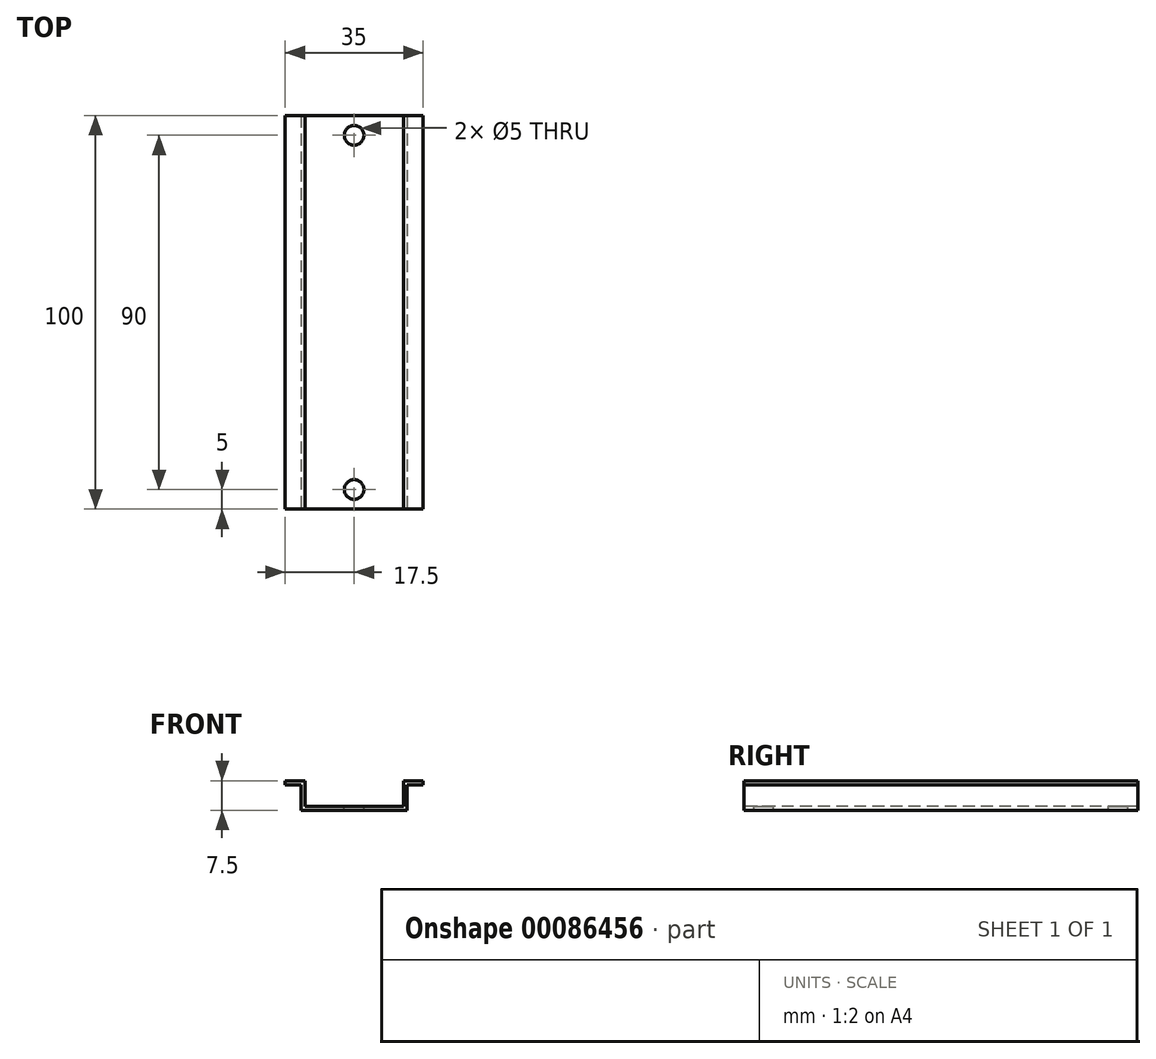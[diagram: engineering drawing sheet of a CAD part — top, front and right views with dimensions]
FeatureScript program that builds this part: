
annotation { "Feature Type Name" : "Feature", "Feature Type Description" : "" }
export const myFeature = defineFeature(function(context is Context, id is Id, definition is map)
    precondition{}
    {
        {
            var Q0;
            Q0=qCreatedBy(makeId("Front.planeOp"),FACE);
            var sketch = newSketch(context, id + "F0", { "sketchPlane" : qUnion([Q0])});
            skLineSegment(sketch, "E0", {"start": v(-17.5, 3.75) * mm, "end": v(-12.5, 3.75) * mm});
            skLineSegment(sketch, "E1", {"start": v(-17.5, 2.75) * mm, "end": v(-17.5, 3.75) * mm});
            skLineSegment(sketch, "E2", {"start": v(-12.5, -2.75) * mm, "end": v(-12.5, 3.75) * mm});
            skLineSegment(sketch, "E3", {"start": v(-13.5, -3.75) * mm, "end": v(-2.6, -3.75) * mm});
            skLineSegment(sketch, "E4", {"start": v(-12.5, -2.75) * mm, "end": v(-2.6, -2.75) * mm});
            skLineSegment(sketch, "E5", {"start": v(-17.5, 2.75) * mm, "end": v(-13.5, 2.75) * mm});
            skLineSegment(sketch, "E6", {"start": v(-13.5, -3.75) * mm, "end": v(-13.5, 2.75) * mm});
            skLineSegment(sketch, "E7", {"start": v(-2.6, -2.75) * mm, "end": v(2.6, -2.75) * mm});
            skLineSegment(sketch, "E8", {"start": v(2.6, -2.75) * mm, "end": v(12.5, -2.75) * mm});
            skLineSegment(sketch, "E9", {"start": v(12.5, -2.75) * mm, "end": v(12.5, 3.75) * mm});
            skLineSegment(sketch, "E10", {"start": v(12.5, 3.75) * mm, "end": v(17.5, 3.75) * mm});
            skLineSegment(sketch, "E11", {"start": v(17.5, 2.75) * mm, "end": v(17.5, 3.75) * mm});
            skLineSegment(sketch, "E12", {"start": v(17.5, 2.75) * mm, "end": v(13.5, 2.75) * mm});
            skLineSegment(sketch, "E13", {"start": v(13.5, -3.75) * mm, "end": v(13.5, 2.75) * mm});
            skLineSegment(sketch, "E14", {"start": v(2.6, -3.75) * mm, "end": v(13.5, -3.75) * mm});
            skLineSegment(sketch, "E15", {"start": v(-2.6, -3.75) * mm, "end": v(2.6, -3.75) * mm});
            skSolve(sketch);
        }
        {
            var Q0;
            Q0=makeQuery(id+"F0.imprint","IMPRINT",FACE,{"disambiguationData":[TD([[makeQuery(id+"F0.imprint","IMPRINT",EDGE,{"derivedFrom":sQuery(id+"F0.wireOp",EDGE,"E0")}),-1.0]])]});
            extrude(context, id + "F1", {"entities" : qUnion([Q0]), "oppositeDirection" : true, "depth" : 100 * mm});
        }
        {
            var Q0;
            Q0=makeQuery(id+"F1.opExtrude","SWEPT_FACE",FACE,{"disambiguationData":[OSD([sQuery(id+"F0.wireOp",EDGE,"E4"),sQuery(id+"F0.wireOp",EDGE,"E7"),sQuery(id+"F0.wireOp",EDGE,"E8")])]});
            var sketch = newSketch(context, id + "F2", { "sketchPlane" : qUnion([Q0])});
            skLineSegment(sketch, "E16", {"start": v(0, 95) * mm, "end": v(0, 5) * mm, "construction": true});
            skCircle(sketch, "E17", {"center": v(0, 100) * mm, "radius": 5 * mm, "construction": true});
            skCircle(sketch, "E18", {"center": v(0, 0) * mm, "radius": 5 * mm, "construction": true});
            skSolve(sketch);
        }
        {
            var Q0;
            Q0=sQuery(id+"F2.wireOp",VERTEX,"E16.start");
            var Q1;
            Q1=sQuery(id+"F2.wireOp",VERTEX,"E16.end");
            var Q2;
            Q2=makeQuery(id+"F1.opExtrude","SWEPT_BODY",BODY,{"disambiguationData":[OSD([sQuery(id+"F0.wireOp",EDGE,"E0"),sQuery(id+"F0.wireOp",EDGE,"E1"),sQuery(id+"F0.wireOp",EDGE,"E2"),sQuery(id+"F0.wireOp",EDGE,"E3"),sQuery(id+"F0.wireOp",EDGE,"E4"),sQuery(id+"F0.wireOp",EDGE,"E5"),sQuery(id+"F0.wireOp",EDGE,"E6"),sQuery(id+"F0.wireOp",EDGE,"E7"),sQuery(id+"F0.wireOp",EDGE,"E8"),sQuery(id+"F0.wireOp",EDGE,"E9"),sQuery(id+"F0.wireOp",EDGE,"E10"),sQuery(id+"F0.wireOp",EDGE,"E11"),sQuery(id+"F0.wireOp",EDGE,"E12"),sQuery(id+"F0.wireOp",EDGE,"E13"),sQuery(id+"F0.wireOp",EDGE,"E14"),sQuery(id+"F0.wireOp",EDGE,"E15")])]});
            hole(context, id + "F3", {"style" : HoleStyle.SIMPLE, "endStyle" : HoleEndStyle.THROUGH, "holeDiameter" : 5 * mm, "startFromSketch" : true, "locations" : qUnion([Q0, Q1]), "scope" : qUnion([Q2]), "isTappedThrough" : true});
        }
    });
